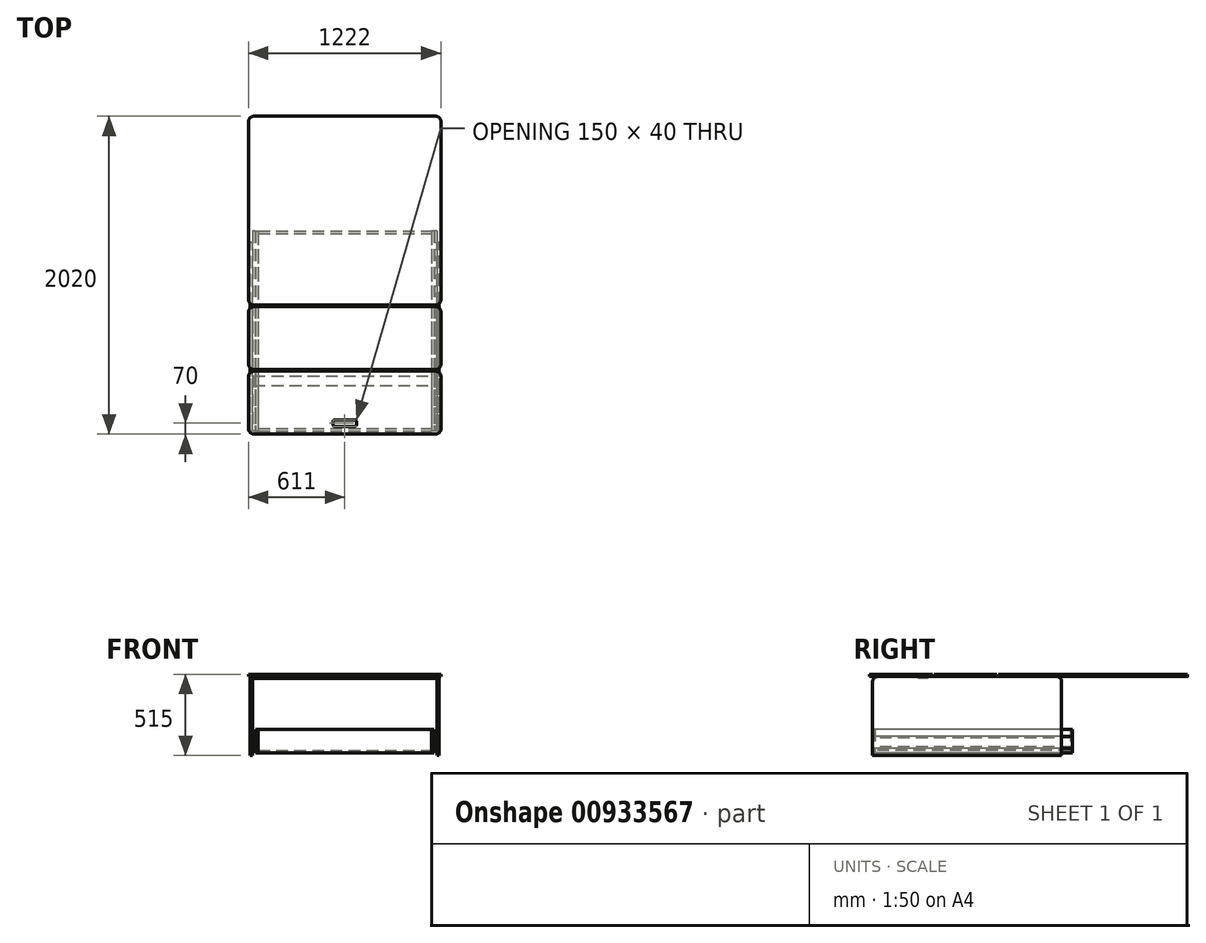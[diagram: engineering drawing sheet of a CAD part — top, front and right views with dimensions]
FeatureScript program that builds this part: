
annotation { "Feature Type Name" : "Feature", "Feature Type Description" : "" }
export const myFeature = defineFeature(function(context is Context, id is Id, definition is map)
    precondition{}
    {
        {
            var Q0;
            Q0=qCreatedBy(makeId("Top.planeOp"),FACE);
            var sketch = newSketch(context, id + "F0", { "sketchPlane" : qUnion([Q0])});
            skLineSegment(sketch, "E0.bottom", {"start": v(600, 0) * mm, "end": v(585, 0) * mm});
            skLineSegment(sketch, "E0.top", {"start": v(600, 1200) * mm, "end": v(585, 1200) * mm, "construction": true});
            skLineSegment(sketch, "E0.left", {"start": v(600, 0) * mm, "end": v(600, 1200) * mm});
            skLineSegment(sketch, "E0.right", {"start": v(585, 0) * mm, "end": v(585, 1200) * mm});
            skLineSegment(sketch, "E1.bottom", {"start": v(-585, 0) * mm, "end": v(-600, 0) * mm});
            skLineSegment(sketch, "E1.top", {"start": v(-585, 1200) * mm, "end": v(-600, 1200) * mm, "construction": true});
            skLineSegment(sketch, "E1.left", {"start": v(-585, 0) * mm, "end": v(-585, 1200) * mm});
            skLineSegment(sketch, "E1.right", {"start": v(-600, 0) * mm, "end": v(-600, 1200) * mm});
            skLineSegment(sketch, "E2", {"start": v(-600, 1200) * mm, "end": v(-585, 1200) * mm});
            skLineSegment(sketch, "E3", {"start": v(585, 1200) * mm, "end": v(600, 1200) * mm});
            skSolve(sketch);
        }
        {
            var Q0;
            Q0 = qSketchRegion(id + "F0", true);
            extrude(context, id + "F1", {"entities" : qUnion([Q0]), "depth" : 500 * mm, "offsetDistance" : 25 * mm});
        }
        {
            var Q0;
            Q0=makeQuery(id+"F1.opExtrude","CAP_EDGE",EDGE,{"disambiguationData":[OSD([sQuery(id+"F0.wireOp",EDGE,"E1.bottom")])],"isStart":false});
            var Q1;
            Q1=makeQuery(id+"F1.opExtrude","CAP_EDGE",EDGE,{"disambiguationData":[OSD([sQuery(id+"F0.wireOp",EDGE,"E2")])],"isStart":false});
            var Q2;
            Q2=makeQuery(id+"F1.opExtrude","CAP_EDGE",EDGE,{"disambiguationData":[OSD([sQuery(id+"F0.wireOp",EDGE,"E3")])],"isStart":false});
            var Q3;
            Q3=makeQuery(id+"F1.opExtrude","CAP_EDGE",EDGE,{"disambiguationData":[OSD([sQuery(id+"F0.wireOp",EDGE,"E0.bottom")])],"isStart":false});
            fillet(context, id + "F2", {"entities" : qUnion([Q0, Q1, Q2, Q3]), "radius" : 30 * mm, "tangentPropagation" : true, "allowEdgeOverflow" : false});
        }
        {
            var Q0;
            Q0=qCreatedBy(makeId("Top.planeOp"),FACE);
            cPlane(context, id + "F3", {"entities" : qUnion([Q0]), "cplaneType" : CPlaneType.OFFSET, "offset" : 500 * mm, "width" : 150 * mm, "height" : 150 * mm});
        }
        {
            var Q0;
            Q0=qCreatedBy(id+"F3.planeOp",FACE);
            var sketch = newSketch(context, id + "F4", { "sketchPlane" : qUnion([Q0])});
            skLineSegment(sketch, "E4.bottom", {"start": v(611, 800) * mm, "end": v(-611, 800) * mm});
            skLineSegment(sketch, "E4.top", {"start": v(611, 2000) * mm, "end": v(-611, 2000) * mm});
            skLineSegment(sketch, "E4.left", {"start": v(611, 800) * mm, "end": v(611, 2000) * mm});
            skLineSegment(sketch, "E4.right", {"start": v(-611, 800) * mm, "end": v(-611, 2000) * mm});
            skSolve(sketch);
        }
        {
            var Q0;
            Q0 = qSketchRegion(id + "F4", true);
            extrude(context, id + "F5", {"entities" : qUnion([Q0]), "depth" : 15 * mm, "offsetDistance" : 25 * mm});
        }
        {
            var Q0;
            Q0=qCreatedBy(id+"F3.planeOp",FACE);
            var sketch = newSketch(context, id + "F6", { "sketchPlane" : qUnion([Q0])});
            skLineSegment(sketch, "E5.bottom", {"start": v(-611, 790) * mm, "end": v(611, 790) * mm});
            skLineSegment(sketch, "E5.top", {"start": v(-611, 390) * mm, "end": v(611, 390) * mm});
            skLineSegment(sketch, "E5.left", {"start": v(-611, 790) * mm, "end": v(-611, 390) * mm});
            skLineSegment(sketch, "E5.right", {"start": v(611, 790) * mm, "end": v(611, 390) * mm});
            skSolve(sketch);
        }
        {
            var Q0;
            Q0 = qSketchRegion(id + "F6", true);
            extrude(context, id + "F7", {"entities" : qUnion([Q0]), "depth" : 15 * mm, "offsetDistance" : 25 * mm});
        }
        {
            var Q0;
            Q0=qCreatedBy(id+"F3.planeOp",FACE);
            var sketch = newSketch(context, id + "F8", { "sketchPlane" : qUnion([Q0])});
            skLineSegment(sketch, "E6.bottom", {"start": v(-611, 380) * mm, "end": v(611, 380) * mm});
            skLineSegment(sketch, "E6.top", {"start": v(-611, -20) * mm, "end": v(611, -20) * mm});
            skLineSegment(sketch, "E6.left", {"start": v(-611, 380) * mm, "end": v(-611, -20) * mm});
            skLineSegment(sketch, "E6.right", {"start": v(611, 380) * mm, "end": v(611, -20) * mm});
            skLineSegment(sketch, "E7.bottom", {"start": v(-75, 30) * mm, "end": v(75, 30) * mm});
            skLineSegment(sketch, "E7.top", {"start": v(-75, 70) * mm, "end": v(75, 70) * mm});
            skLineSegment(sketch, "E7.left", {"start": v(-75, 30) * mm, "end": v(-75, 70) * mm});
            skLineSegment(sketch, "E7.right", {"start": v(75, 30) * mm, "end": v(75, 70) * mm});
            skSolve(sketch);
        }
        {
            var Q0;
            Q0 = qSketchRegion(id + "F8", true);
            extrude(context, id + "F9", {"entities" : qUnion([Q0]), "depth" : 15 * mm, "offsetDistance" : 25 * mm});
        }
        {
            var Q0;
            Q0=makeQuery(id+"F9.opExtrude","SWEPT_EDGE",EDGE,{"disambiguationData":[OSD([sQuery(id+"F8.wireOp",EDGE,"E7.top"),sQuery(id+"F8.wireOp",EDGE,"E7.left")])]});
            var Q1;
            Q1=makeQuery(id+"F9.opExtrude","SWEPT_EDGE",EDGE,{"disambiguationData":[OSD([sQuery(id+"F8.wireOp",EDGE,"E7.top"),sQuery(id+"F8.wireOp",EDGE,"E7.right")])]});
            var Q2;
            Q2=makeQuery(id+"F9.opExtrude","SWEPT_EDGE",EDGE,{"disambiguationData":[OSD([sQuery(id+"F8.wireOp",EDGE,"E7.bottom"),sQuery(id+"F8.wireOp",EDGE,"E7.right")])]});
            var Q3;
            Q3=makeQuery(id+"F9.opExtrude","SWEPT_EDGE",EDGE,{"disambiguationData":[OSD([sQuery(id+"F8.wireOp",EDGE,"E7.bottom"),sQuery(id+"F8.wireOp",EDGE,"E7.left")])]});
            fillet(context, id + "F10", {"entities" : qUnion([Q0, Q1, Q2, Q3]), "radius" : 10 * mm, "tangentPropagation" : true, "allowEdgeOverflow" : false});
        }
        {
            var Q0;
            Q0=makeQuery(id+"F9.opExtrude","SWEPT_EDGE",EDGE,{"disambiguationData":[OSD([sQuery(id+"F8.wireOp",EDGE,"E6.top"),sQuery(id+"F8.wireOp",EDGE,"E6.right")])]});
            var Q1;
            Q1=makeQuery(id+"F9.opExtrude","SWEPT_EDGE",EDGE,{"disambiguationData":[OSD([sQuery(id+"F8.wireOp",EDGE,"E6.top"),sQuery(id+"F8.wireOp",EDGE,"E6.left")])]});
            var Q2;
            Q2=makeQuery(id+"F5.opExtrude","SWEPT_EDGE",EDGE,{"disambiguationData":[OSD([sQuery(id+"F4.wireOp",EDGE,"E4.top"),sQuery(id+"F4.wireOp",EDGE,"E4.right")])]});
            var Q3;
            Q3=makeQuery(id+"F5.opExtrude","SWEPT_EDGE",EDGE,{"disambiguationData":[OSD([sQuery(id+"F4.wireOp",EDGE,"E4.top"),sQuery(id+"F4.wireOp",EDGE,"E4.left")])]});
            var Q4;
            Q4=makeQuery(id+"F5.opExtrude","SWEPT_EDGE",EDGE,{"disambiguationData":[OSD([sQuery(id+"F4.wireOp",EDGE,"E4.bottom"),sQuery(id+"F4.wireOp",EDGE,"E4.left")])]});
            var Q5;
            Q5=makeQuery(id+"F7.opExtrude","SWEPT_EDGE",EDGE,{"disambiguationData":[OSD([sQuery(id+"F6.wireOp",EDGE,"E5.bottom"),sQuery(id+"F6.wireOp",EDGE,"E5.right")])]});
            var Q6;
            Q6=makeQuery(id+"F9.opExtrude","SWEPT_EDGE",EDGE,{"disambiguationData":[OSD([sQuery(id+"F8.wireOp",EDGE,"E6.bottom"),sQuery(id+"F8.wireOp",EDGE,"E6.right")])]});
            var Q7;
            Q7=makeQuery(id+"F7.opExtrude","SWEPT_EDGE",EDGE,{"disambiguationData":[OSD([sQuery(id+"F6.wireOp",EDGE,"E5.top"),sQuery(id+"F6.wireOp",EDGE,"E5.right")])]});
            var Q8;
            Q8=makeQuery(id+"F5.opExtrude","SWEPT_EDGE",EDGE,{"disambiguationData":[OSD([sQuery(id+"F4.wireOp",EDGE,"E4.bottom"),sQuery(id+"F4.wireOp",EDGE,"E4.right")])]});
            var Q9;
            Q9=makeQuery(id+"F7.opExtrude","SWEPT_EDGE",EDGE,{"disambiguationData":[OSD([sQuery(id+"F6.wireOp",EDGE,"E5.bottom"),sQuery(id+"F6.wireOp",EDGE,"E5.left")])]});
            var Q10;
            Q10=makeQuery(id+"F9.opExtrude","SWEPT_EDGE",EDGE,{"disambiguationData":[OSD([sQuery(id+"F8.wireOp",EDGE,"E6.bottom"),sQuery(id+"F8.wireOp",EDGE,"E6.left")])]});
            var Q11;
            Q11=makeQuery(id+"F7.opExtrude","SWEPT_EDGE",EDGE,{"disambiguationData":[OSD([sQuery(id+"F6.wireOp",EDGE,"E5.top"),sQuery(id+"F6.wireOp",EDGE,"E5.left")])]});
            fillet(context, id + "F11", {"entities" : qUnion([Q0, Q1, Q2, Q3, Q4, Q5, Q6, Q7, Q8, Q9, Q10, Q11]), "radius" : 35 * mm, "tangentPropagation" : true, "allowEdgeOverflow" : false});
        }
        {
            var Q0;
            Q0=qCreatedBy(makeId("Top.planeOp"),FACE);
            cPlane(context, id + "F12", {"entities" : qUnion([Q0]), "cplaneType" : CPlaneType.OFFSET, "offset" : 15 * mm, "width" : 150 * mm, "height" : 150 * mm});
        }
        {
            var Q0;
            Q0=qCreatedBy(id+"F12.planeOp",FACE);
            var sketch = newSketch(context, id + "F13", { "sketchPlane" : qUnion([Q0])});
            skLineSegment(sketch, "E8.bottom", {"start": v(-550.6, 1255) * mm, "end": v(550.6, 1255) * mm});
            skLineSegment(sketch, "E8.top", {"start": v(-550.6, 15) * mm, "end": v(550.6, 15) * mm});
            skLineSegment(sketch, "E8.left", {"start": v(-550.6, 1255) * mm, "end": v(-550.6, 15) * mm});
            skLineSegment(sketch, "E8.right", {"start": v(550.6, 1255) * mm, "end": v(550.6, 15) * mm});
            skSolve(sketch);
        }
        {
            var Q0;
            Q0=makeQuery(id+"F13.imprint","IMPRINT",FACE,{"disambiguationData":[TD([[makeQuery(id+"F13.imprint","IMPRINT",EDGE,{"derivedFrom":sQuery(id+"F13.wireOp",EDGE,"E8.bottom")}),-1.0]])]});
            extrude(context, id + "F14", {"entities" : qUnion([Q0]), "depth" : 15 * mm, "offsetDistance" : 25 * mm});
        }
        {
            var Q0;
            Q0=qCreatedBy(makeId("Front.planeOp"),FACE);
            var sketch = newSketch(context, id + "F15", { "sketchPlane" : qUnion([Q0])});
            skLineSegment(sketch, "E9.bottom", {"start": v(-550.6, 165) * mm, "end": v(550.6, 165) * mm});
            skLineSegment(sketch, "E9.top", {"start": v(-550.6, 15) * mm, "end": v(550.6, 15) * mm});
            skLineSegment(sketch, "E9.left", {"start": v(-550.6, 165) * mm, "end": v(-550.6, 15) * mm});
            skLineSegment(sketch, "E9.right", {"start": v(550.6, 165) * mm, "end": v(550.6, 15) * mm});
            skSolve(sketch);
        }
        {
            var Q0;
            Q0 = qSketchRegion(id + "F15", true);
            extrude(context, id + "F16", {"entities" : qUnion([Q0]), "oppositeDirection" : true, "depth" : 15 * mm, "offsetDistance" : 25 * mm});
        }
        {
            var Q0;
            Q0=makeQuery(id+"F14.opExtrude","SWEPT_FACE",FACE,{"disambiguationData":[OSD([sQuery(id+"F13.wireOp",EDGE,"E8.bottom")])]});
            var sketch = newSketch(context, id + "F17", { "sketchPlane" : qUnion([Q0])});
            skLineSegment(sketch, "E10.bottom", {"start": v(-550.6, 15) * mm, "end": v(550.6, 15) * mm});
            skLineSegment(sketch, "E10.top", {"start": v(-550.6, 165) * mm, "end": v(550.6, 165) * mm});
            skLineSegment(sketch, "E10.left", {"start": v(-550.6, 15) * mm, "end": v(-550.6, 165) * mm});
            skLineSegment(sketch, "E10.right", {"start": v(550.6, 15) * mm, "end": v(550.6, 165) * mm});
            skSolve(sketch);
        }
        {
            var Q0;
            Q0 = qSketchRegion(id + "F17", true);
            extrude(context, id + "F18", {"entities" : qUnion([Q0]), "depth" : 15 * mm, "offsetDistance" : 25 * mm});
        }
        {
            var Q0;
            Q0=makeQuery(id+"F14.opExtrude","SWEPT_FACE",FACE,{"disambiguationData":[OSD([sQuery(id+"F13.wireOp",EDGE,"E8.right")])]});
            var sketch = newSketch(context, id + "F19", { "sketchPlane" : qUnion([Q0])});
            skLineSegment(sketch, "E11.bottom", {"start": v(1270, 15) * mm, "end": v(0, 15) * mm});
            skLineSegment(sketch, "E11.top", {"start": v(1270, 165) * mm, "end": v(0, 165) * mm});
            skLineSegment(sketch, "E11.left", {"start": v(1270, 15) * mm, "end": v(1270, 165) * mm});
            skLineSegment(sketch, "E11.right", {"start": v(0, 15) * mm, "end": v(0, 165) * mm});
            skSolve(sketch);
        }
        {
            var Q0;
            Q0 = qSketchRegion(id + "F19", true);
            extrude(context, id + "F20", {"entities" : qUnion([Q0]), "depth" : 15 * mm, "offsetDistance" : 25 * mm});
        }
        {
            var Q0;
            Q0=makeQuery(id+"F14.opExtrude","SWEPT_FACE",FACE,{"disambiguationData":[OSD([sQuery(id+"F13.wireOp",EDGE,"E8.left")])]});
            var sketch = newSketch(context, id + "F21", { "sketchPlane" : qUnion([Q0])});
            skLineSegment(sketch, "E12.bottom", {"start": v(-1270, 165) * mm, "end": v(0, 165) * mm});
            skLineSegment(sketch, "E12.top", {"start": v(-1270, 15) * mm, "end": v(0, 15) * mm});
            skLineSegment(sketch, "E12.left", {"start": v(-1270, 165) * mm, "end": v(-1270, 15) * mm});
            skLineSegment(sketch, "E12.right", {"start": v(0, 165) * mm, "end": v(0, 15) * mm});
            skSolve(sketch);
        }
        {
            var Q0;
            Q0 = qSketchRegion(id + "F21", true);
            extrude(context, id + "F22", {"entities" : qUnion([Q0]), "depth" : 15 * mm, "offsetDistance" : 25 * mm});
        }
        {
            var Q0;
            Q0=qCreatedBy(makeId("Front.planeOp"),FACE);
            var sketch = newSketch(context, id + "F23", { "sketchPlane" : qUnion([Q0])});
            skLineSegment(sketch, "E13.bottom", {"start": v(579, 45) * mm, "end": v(576, 45) * mm});
            skLineSegment(sketch, "E13.top", {"start": v(579, 121.2) * mm, "end": v(576, 121.2) * mm});
            skLineSegment(sketch, "E13.left", {"start": v(585, 51) * mm, "end": v(585, 115.2) * mm});
            skLineSegment(sketch, "E13.right", {"start": v(570, 51) * mm, "end": v(570, 115.2) * mm});
            skLineSegment(sketch, "E14.bottom", {"start": v(570, 55) * mm, "end": v(567.9, 55) * mm});
            skLineSegment(sketch, "E14.top", {"start": v(570, 111.2) * mm, "end": v(567.9, 111.2) * mm});
            skLineSegment(sketch, "E14.left", {"start": v(570, 55) * mm, "end": v(570, 111.2) * mm});
            skLineSegment(sketch, "E14.right", {"start": v(565.9, 57) * mm, "end": v(565.9, 109.2) * mm});
            skPoint(sketch, "E15.visualSharp", {"position": v(585, 45) * mm});
            skArc(sketch, "E15.filletArc", {"start": v(579, 45) * mm, "mid": v(583.24, 46.76) * mm, "end": v(585, 51) * mm});
            skPoint(sketch, "E16.visualSharp", {"position": v(585, 121.2) * mm});
            skArc(sketch, "E16.filletArc", {"start": v(585, 115.2) * mm, "mid": v(583.24, 119.44) * mm, "end": v(579, 121.2) * mm});
            skPoint(sketch, "E17.visualSharp", {"position": v(565.9, 111.2) * mm});
            skArc(sketch, "E17.filletArc", {"start": v(567.9, 111.2) * mm, "mid": v(566.49, 110.61) * mm, "end": v(565.9, 109.2) * mm});
            skPoint(sketch, "E18.visualSharp", {"position": v(565.9, 55) * mm});
            skArc(sketch, "E18.filletArc", {"start": v(565.9, 57) * mm, "mid": v(566.49, 55.59) * mm, "end": v(567.9, 55) * mm});
            skPoint(sketch, "E19.visualSharp", {"position": v(570, 121.2) * mm});
            skArc(sketch, "E19.filletArc", {"start": v(576, 121.2) * mm, "mid": v(571.76, 119.44) * mm, "end": v(570, 115.2) * mm});
            skPoint(sketch, "E20.visualSharp", {"position": v(570, 45) * mm});
            skArc(sketch, "E20.filletArc", {"start": v(570, 51) * mm, "mid": v(571.76, 46.76) * mm, "end": v(576, 45) * mm});
            skLineSegment(sketch, "E21", {"start": v(0, 0) * mm, "end": v(0, 269.37) * mm, "construction": true});
            skArc(sketch, "E22.MirrorCS", {"start": v(-565.9, 57) * mm, "mid": v(-566.49, 55.59) * mm, "end": v(-567.9, 55) * mm});
            skLineSegment(sketch, "E23.MirrorCS", {"start": v(-570, 55) * mm, "end": v(-567.9, 55) * mm});
            skArc(sketch, "E24.MirrorCS", {"start": v(-567.9, 111.2) * mm, "mid": v(-566.49, 110.61) * mm, "end": v(-565.9, 109.2) * mm});
            skLineSegment(sketch, "E25.MirrorCS", {"start": v(-570, 111.2) * mm, "end": v(-567.9, 111.2) * mm});
            skArc(sketch, "E26.MirrorCS", {"start": v(-570, 51) * mm, "mid": v(-571.76, 46.76) * mm, "end": v(-576, 45) * mm});
            skLineSegment(sketch, "E27.MirrorCS", {"start": v(-579, 121.2) * mm, "end": v(-576, 121.2) * mm});
            skLineSegment(sketch, "E28.MirrorCS", {"start": v(-579, 45) * mm, "end": v(-576, 45) * mm});
            skArc(sketch, "E29.MirrorCS", {"start": v(-585, 115.2) * mm, "mid": v(-583.24, 119.44) * mm, "end": v(-579, 121.2) * mm});
            skArc(sketch, "E30.MirrorCS", {"start": v(-579, 45) * mm, "mid": v(-583.24, 46.76) * mm, "end": v(-585, 51) * mm});
            skArc(sketch, "E31.MirrorCS", {"start": v(-576, 121.2) * mm, "mid": v(-571.76, 119.44) * mm, "end": v(-570, 115.2) * mm});
            skLineSegment(sketch, "E32.MirrorCS", {"start": v(-570, 55) * mm, "end": v(-570, 111.2) * mm});
            skPoint(sketch, "E33.MirrorP", {"position": v(-570, 45) * mm});
            skLineSegment(sketch, "E34.MirrorCS", {"start": v(-565.9, 57) * mm, "end": v(-565.9, 109.2) * mm});
            skPoint(sketch, "E35.MirrorP", {"position": v(-585, 121.2) * mm});
            skPoint(sketch, "E36.MirrorP", {"position": v(-565.9, 111.2) * mm});
            skPoint(sketch, "E37.MirrorP", {"position": v(-585, 45) * mm});
            skPoint(sketch, "E38.MirrorP", {"position": v(-570, 121.2) * mm});
            skPoint(sketch, "E39.MirrorP", {"position": v(-565.9, 55) * mm});
            skLineSegment(sketch, "E40.MirrorCS", {"start": v(-570, 51) * mm, "end": v(-570, 115.2) * mm});
            skLineSegment(sketch, "E41.MirrorCS", {"start": v(-585, 51) * mm, "end": v(-585, 115.2) * mm});
            skSolve(sketch);
        }
        {
            var Q0;
            Q0 = qSketchRegion(id + "F23", true);
            extrude(context, id + "F24", {"entities" : qUnion([Q0]), "oppositeDirection" : true, "depth" : 1270 * mm, "offsetDistance" : 25 * mm});
        }
        {
            var Q0;
            Q0=makeQuery(id+"F9.opExtrude","CAP_FACE",FACE,{"disambiguationData":[OSD([sQuery(id+"F8.wireOp",EDGE,"E6.bottom"),sQuery(id+"F8.wireOp",EDGE,"E6.top"),sQuery(id+"F8.wireOp",EDGE,"E6.left"),sQuery(id+"F8.wireOp",EDGE,"E6.right"),sQuery(id+"F8.wireOp",EDGE,"E7.bottom"),sQuery(id+"F8.wireOp",EDGE,"E7.top"),sQuery(id+"F8.wireOp",EDGE,"E7.left"),sQuery(id+"F8.wireOp",EDGE,"E7.right")])],"isStart":true});
            var sketch = newSketch(context, id + "F25", { "sketchPlane" : qUnion([Q0])});
            skLineSegment(sketch, "E42.bottom", {"start": v(-580, -350) * mm, "end": v(580, -350) * mm});
            skLineSegment(sketch, "E42.top", {"start": v(-580, -290) * mm, "end": v(580, -290) * mm});
            skLineSegment(sketch, "E42.left", {"start": v(-580, -350) * mm, "end": v(-580, -290) * mm});
            skLineSegment(sketch, "E42.right", {"start": v(580, -350) * mm, "end": v(580, -290) * mm});
            skSolve(sketch);
        }
        {
            var Q0;
            Q0 = qSketchRegion(id + "F25", true);
            extrude(context, id + "F26", {"entities" : qUnion([Q0]), "depth" : 12 * mm, "offsetDistance" : 25 * mm});
        }
    });
